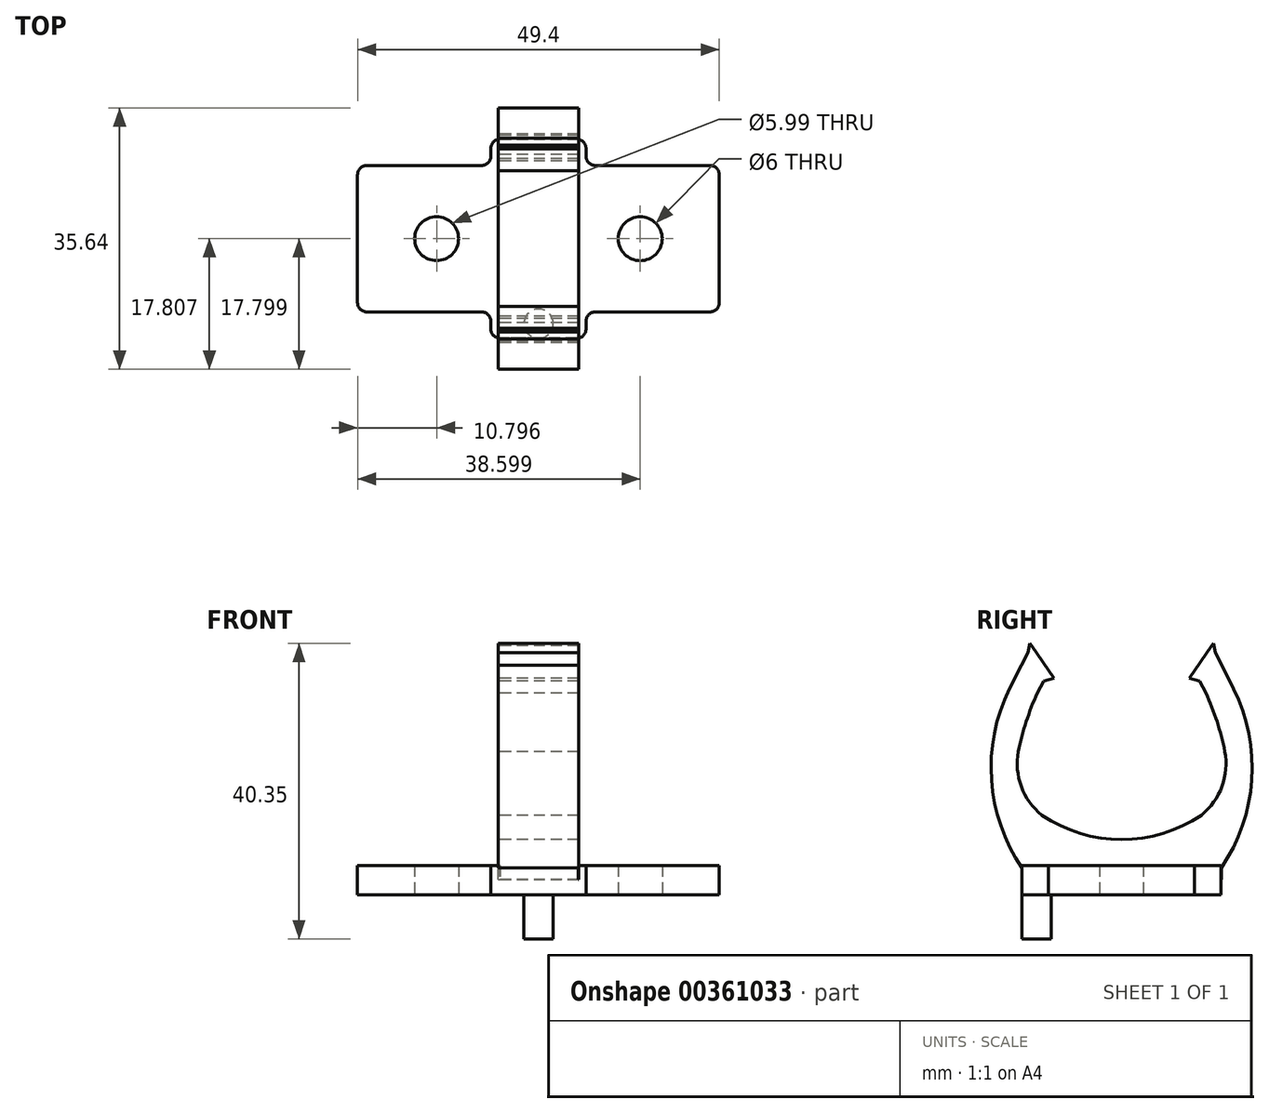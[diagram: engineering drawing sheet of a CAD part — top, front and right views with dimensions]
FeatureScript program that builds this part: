
annotation { "Feature Type Name" : "Feature", "Feature Type Description" : "" }
export const myFeature = defineFeature(function(context is Context, id is Id, definition is map)
    precondition{}
    {
        {
            var Q0;
            Q0=qCreatedBy(makeId("Top.planeOp"),FACE);
            var sketch = newSketch(context, id + "F0", { "sketchPlane" : qUnion([Q0])});
            skLineSegment(sketch, "E0", {"start": v(-41.32, 24.59) * mm, "end": v(-25.66, 24.59) * mm});
            skLineSegment(sketch, "E1", {"start": v(-24.4, 25.86) * mm, "end": v(-24.4, 26.92) * mm});
            skLineSegment(sketch, "E2", {"start": v(-23.12, 28.19) * mm, "end": v(-12.66, 28.19) * mm});
            skLineSegment(sketch, "E3", {"start": v(-11.4, 26.92) * mm, "end": v(-11.4, 25.86) * mm});
            skLineSegment(sketch, "E4", {"start": v(-10.12, 24.59) * mm, "end": v(5.54, 24.59) * mm});
            skLineSegment(sketch, "E5", {"start": v(6.8, 23.32) * mm, "end": v(6.8, 5.86) * mm});
            skLineSegment(sketch, "E6", {"start": v(5.54, 4.59) * mm, "end": v(-10.12, 4.59) * mm});
            skLineSegment(sketch, "E7", {"start": v(-11.4, 3.32) * mm, "end": v(-11.4, 2.26) * mm});
            skLineSegment(sketch, "E8", {"start": v(-12.66, 0.99) * mm, "end": v(-23.12, 0.99) * mm});
            skLineSegment(sketch, "E9", {"start": v(-24.4, 2.26) * mm, "end": v(-24.4, 3.32) * mm});
            skLineSegment(sketch, "E10", {"start": v(-25.66, 4.59) * mm, "end": v(-41.32, 4.59) * mm});
            skLineSegment(sketch, "E11", {"start": v(-42.6, 5.86) * mm, "end": v(-42.6, 23.32) * mm});
            skCircle(sketch, "E12", {"center": v(-4, 14.59) * mm, "radius": 3 * mm});
            skCircle(sketch, "E13", {"center": v(-31.8, 14.6) * mm, "radius": 3 * mm});
            skPoint(sketch, "E14.visualSharp", {"position": v(-42.6, 24.59) * mm});
            skArc(sketch, "E14.filletArc", {"start": v(-41.32, 24.59) * mm, "mid": v(-42.22, 24.22) * mm, "end": v(-42.6, 23.32) * mm});
            skPoint(sketch, "E15.visualSharp", {"position": v(-42.6, 4.59) * mm});
            skArc(sketch, "E15.filletArc", {"start": v(-42.6, 5.86) * mm, "mid": v(-42.22, 4.96) * mm, "end": v(-41.32, 4.59) * mm});
            skPoint(sketch, "E16.visualSharp", {"position": v(-24.4, 4.59) * mm});
            skArc(sketch, "E16.filletArc", {"start": v(-24.4, 3.32) * mm, "mid": v(-24.76, 4.22) * mm, "end": v(-25.66, 4.59) * mm});
            skPoint(sketch, "E17.visualSharp", {"position": v(-24.4, 0.99) * mm});
            skArc(sketch, "E17.filletArc", {"start": v(-24.4, 2.26) * mm, "mid": v(-24.02, 1.36) * mm, "end": v(-23.12, 0.99) * mm});
            skPoint(sketch, "E18.visualSharp", {"position": v(-11.4, 0.99) * mm});
            skArc(sketch, "E18.filletArc", {"start": v(-12.66, 0.99) * mm, "mid": v(-11.76, 1.36) * mm, "end": v(-11.4, 2.26) * mm});
            skPoint(sketch, "E19.visualSharp", {"position": v(-11.4, 4.59) * mm});
            skArc(sketch, "E19.filletArc", {"start": v(-10.12, 4.59) * mm, "mid": v(-11.02, 4.22) * mm, "end": v(-11.4, 3.32) * mm});
            skPoint(sketch, "E20.visualSharp", {"position": v(6.8, 4.59) * mm});
            skArc(sketch, "E20.filletArc", {"start": v(5.54, 4.59) * mm, "mid": v(6.44, 4.96) * mm, "end": v(6.8, 5.86) * mm});
            skPoint(sketch, "E21.visualSharp", {"position": v(6.8, 24.59) * mm});
            skArc(sketch, "E21.filletArc", {"start": v(6.8, 23.32) * mm, "mid": v(6.44, 24.22) * mm, "end": v(5.54, 24.59) * mm});
            skPoint(sketch, "E22.visualSharp", {"position": v(-11.4, 24.59) * mm});
            skArc(sketch, "E22.filletArc", {"start": v(-11.4, 25.86) * mm, "mid": v(-11.02, 24.96) * mm, "end": v(-10.12, 24.59) * mm});
            skPoint(sketch, "E23.visualSharp", {"position": v(-11.4, 28.19) * mm});
            skArc(sketch, "E23.filletArc", {"start": v(-11.4, 26.92) * mm, "mid": v(-11.76, 27.82) * mm, "end": v(-12.66, 28.19) * mm});
            skPoint(sketch, "E24.visualSharp", {"position": v(-24.4, 28.19) * mm});
            skArc(sketch, "E24.filletArc", {"start": v(-23.12, 28.19) * mm, "mid": v(-24.02, 27.82) * mm, "end": v(-24.4, 26.92) * mm});
            skPoint(sketch, "E25.visualSharp", {"position": v(-24.4, 24.59) * mm});
            skArc(sketch, "E25.filletArc", {"start": v(-25.66, 24.59) * mm, "mid": v(-24.76, 24.96) * mm, "end": v(-24.4, 25.86) * mm});
            skLineSegment(sketch, "E26", {"start": v(-17.9, 0.99) * mm, "end": v(-17.9, 28.19) * mm});
            skSolve(sketch);
        }
        {
            var Q0;
            Q0=makeQuery(id+"F0.imprint","IMPRINT",FACE,{"disambiguationData":[TD([[makeQuery(id+"F0.imprint","IMPRINT",EDGE,{"derivedFrom":sQuery(id+"F0.wireOp",EDGE,"E0")}),-1.0]])]});
            var Q1;
            Q1=makeQuery(id+"F0.imprint","IMPRINT",FACE,{"disambiguationData":[TD([[makeQuery(id+"F0.imprint","IMPRINT",EDGE,{"derivedFrom":sQuery(id+"F0.wireOp",EDGE,"E3")}),-1.0]])]});
            extrude(context, id + "F1", {"entities" : qUnion([Q0, Q1]), "depth" : 4 * mm});
        }
        {
            var Q0;
            Q0=qCreatedBy(makeId("Right.planeOp"),FACE);
            cPlane(context, id + "F2", {"entities" : qUnion([Q0]), "cplaneType" : CPlaneType.OFFSET, "offset" : 17.9 * mm, "oppositeDirection" : true, "width" : 152.4 * mm, "height" : 152.4 * mm});
        }
        {
            var Q0;
            Q0=qCreatedBy(id+"F2.planeOp",FACE);
            var sketch = newSketch(context, id + "F3", { "sketchPlane" : qUnion([Q0])});
            skLineSegment(sketch, "E27", {"start": v(1.01, 2.1) * mm, "end": v(28.22, 2.1) * mm});
            skLineSegment(sketch, "E28", {"start": v(14.61, 0) * mm, "end": v(14.61, 40.9) * mm});
            skPoint(sketch, "E28.startSnap0", {"position": v(14.61, 2.1) * mm});
            skArc(sketch, "E29", {"start": v(28.71, 19.6) * mm, "mid": v(27.64, 23.67) * mm, "end": v(26.12, 27.6) * mm});
            skArc(sketch, "E30", {"start": v(25.51, 10.9) * mm, "mid": v(28.3, 14.8) * mm, "end": v(28.71, 19.6) * mm});
            skLineSegment(sketch, "E31", {"start": v(29.91, 28.16) * mm, "end": v(28.31, 31.4) * mm});
            skLineSegment(sketch, "E32", {"start": v(28.22, 2.1) * mm, "end": v(28.22, 3.67) * mm});
            skArc(sketch, "E33", {"start": v(28.22, 3.67) * mm, "mid": v(32.38, 15.69) * mm, "end": v(29.91, 28.16) * mm});
            skLineSegment(sketch, "E34.MirrorCS", {"start": v(1.01, 2.1) * mm, "end": v(1.01, 3.67) * mm});
            skLineSegment(sketch, "E35.MirrorCS", {"start": v(-0.69, 28.16) * mm, "end": v(0.91, 31.4) * mm});
            skLineSegment(sketch, "E36.MirrorCS", {"start": v(28.22, 2.1) * mm, "end": v(1.01, 2.1) * mm});
            skArc(sketch, "E37.MirrorCS", {"start": v(3.71, 10.9) * mm, "mid": v(0.92, 14.8) * mm, "end": v(0.51, 19.6) * mm});
            skArc(sketch, "E38.MirrorCS", {"start": v(0.51, 19.6) * mm, "mid": v(1.59, 23.67) * mm, "end": v(3.1, 27.6) * mm});
            skArc(sketch, "E39.MirrorCS", {"start": v(1.01, 3.67) * mm, "mid": v(-3.15, 15.69) * mm, "end": v(-0.69, 28.16) * mm});
            skArc(sketch, "E40", {"start": v(3.71, 10.9) * mm, "mid": v(14.61, 7.57) * mm, "end": v(25.51, 10.9) * mm});
            skLineSegment(sketch, "E41", {"start": v(26.9, 34.05) * mm, "end": v(23.87, 29.62) * mm});
            skLineSegment(sketch, "E42", {"start": v(23.87, 29.62) * mm, "end": v(25.24, 29.25) * mm});
            skLineSegment(sketch, "E43", {"start": v(26.12, 27.6) * mm, "end": v(25.24, 29.25) * mm});
            skLineSegment(sketch, "E44", {"start": v(26.9, 34.05) * mm, "end": v(27.14, 34.35) * mm});
            skLineSegment(sketch, "E45", {"start": v(27.14, 34.35) * mm, "end": v(27.4, 33.1) * mm});
            skLineSegment(sketch, "E46", {"start": v(27.4, 33.1) * mm, "end": v(28.31, 31.4) * mm});
            skLineSegment(sketch, "E47.MirrorCS", {"start": v(2.09, 34.35) * mm, "end": v(1.83, 33.1) * mm});
            skLineSegment(sketch, "E48.MirrorCS", {"start": v(3.1, 27.6) * mm, "end": v(4, 29.25) * mm});
            skLineSegment(sketch, "E49.MirrorCS", {"start": v(5.36, 29.62) * mm, "end": v(4, 29.25) * mm});
            skLineSegment(sketch, "E50.MirrorCS", {"start": v(1.83, 33.1) * mm, "end": v(0.91, 31.4) * mm});
            skLineSegment(sketch, "E51.MirrorCS", {"start": v(2.33, 34.05) * mm, "end": v(2.09, 34.35) * mm});
            skLineSegment(sketch, "E52.MirrorCS", {"start": v(2.33, 34.05) * mm, "end": v(5.36, 29.62) * mm});
            skSolve(sketch);
        }
        {
            var Q0;
            Q0 = qSketchRegion(id + "F3", true);
            extrude(context, id + "F4", {"entities" : qUnion([Q0]), "operationType" : NewBodyOperationType.ADD, "depth" : 5.5 * mm});
        }
        {
            var Q0;
            Q0=makeQuery(id+"F4.opExtrude","CAP_FACE",FACE,{"disambiguationData":[OSD([sQuery(id+"F3.wireOp",EDGE,"E29"),sQuery(id+"F3.wireOp",EDGE,"E30"),sQuery(id+"F3.wireOp",EDGE,"E31"),sQuery(id+"F3.wireOp",EDGE,"E32"),sQuery(id+"F3.wireOp",EDGE,"E33"),sQuery(id+"F3.wireOp",EDGE,"E34.MirrorCS"),sQuery(id+"F3.wireOp",EDGE,"E36.MirrorCS"),sQuery(id+"F3.wireOp",EDGE,"E40"),sQuery(id+"F3.wireOp",EDGE,"E41"),sQuery(id+"F3.wireOp",EDGE,"E42"),sQuery(id+"F3.wireOp",EDGE,"E43"),sQuery(id+"F3.wireOp",EDGE,"E44"),sQuery(id+"F3.wireOp",EDGE,"E45"),sQuery(id+"F3.wireOp",EDGE,"E46"),sQuery(id+"F3.wireOp",EDGE,"E47.MirrorCS"),sQuery(id+"F3.wireOp",EDGE,"E48.MirrorCS"),sQuery(id+"F3.wireOp",EDGE,"E49.MirrorCS"),sQuery(id+"F3.wireOp",EDGE,"E50.MirrorCS"),sQuery(id+"F3.wireOp",EDGE,"E51.MirrorCS"),sQuery(id+"F3.wireOp",EDGE,"E38.MirrorCS"),sQuery(id+"F3.wireOp",EDGE,"E37.MirrorCS"),sQuery(id+"F3.wireOp",EDGE,"E39.MirrorCS"),sQuery(id+"F3.wireOp",EDGE,"E35.MirrorCS"),sQuery(id+"F3.wireOp",EDGE,"E52.MirrorCS")])],"isStart":true});
            extrude(context, id + "F5", {"entities" : qUnion([Q0]), "operationType" : NewBodyOperationType.ADD, "depth" : 5.5 * mm});
        }
        {
            var Q0;
            Q0=makeQuery(id+"F0.imprint","IMPRINT",FACE,{"disambiguationData":[TD([[makeQuery(id+"F0.imprint","IMPRINT",EDGE,{"derivedFrom":sQuery(id+"F0.wireOp",EDGE,"E0")}),-1.0]])]});
            var sketch = newSketch(context, id + "F6", { "sketchPlane" : qUnion([Q0])});
            skCircle(sketch, "E53", {"center": v(-17.87, 2.99) * mm, "radius": 2 * mm});
            skSolve(sketch);
        }
        {
            var Q0;
            {var subQ0=sQuery(id+"F6.wireOp",EDGE,"E53");var subQ1=makeQuery(id+"F0.imprint","IMPRINT",EDGE,{"derivedFrom":sQuery(id+"F0.wireOp",EDGE,"E26")});var subQ2=makeQuery(id+"F6.imprint","INTERSECT",VERTEX,{"disambiguationData":[OD(0.0)],"derivedFrom":[subQ1,subQ0]});Q0=makeQuery(id+"F6.imprint","IMPRINT",FACE,{"disambiguationData":[TD([[makeQuery(id+"F6.imprint","IMPRINT",EDGE,{"disambiguationData":[TD([[subQ2,-1.0]])],"derivedFrom":subQ0}),1.0]])]});}
            var Q1;
            {var subQ0=sQuery(id+"F6.wireOp",EDGE,"E53");var subQ1=makeQuery(id+"F0.imprint","IMPRINT",EDGE,{"derivedFrom":sQuery(id+"F0.wireOp",EDGE,"E26")});var subQ2=makeQuery(id+"F6.imprint","INTERSECT",VERTEX,{"disambiguationData":[OD(0.0)],"derivedFrom":[subQ1,subQ0]});Q1=makeQuery(id+"F6.imprint","IMPRINT",FACE,{"disambiguationData":[TD([[makeQuery(id+"F6.imprint","IMPRINT",EDGE,{"disambiguationData":[TD([[subQ2,1.0]])],"derivedFrom":subQ0}),1.0]])]});}
            extrude(context, id + "F7", {"entities" : qUnion([Q0, Q1]), "operationType" : NewBodyOperationType.ADD, "oppositeDirection" : true, "depth" : 6 * mm});
        }
    });
